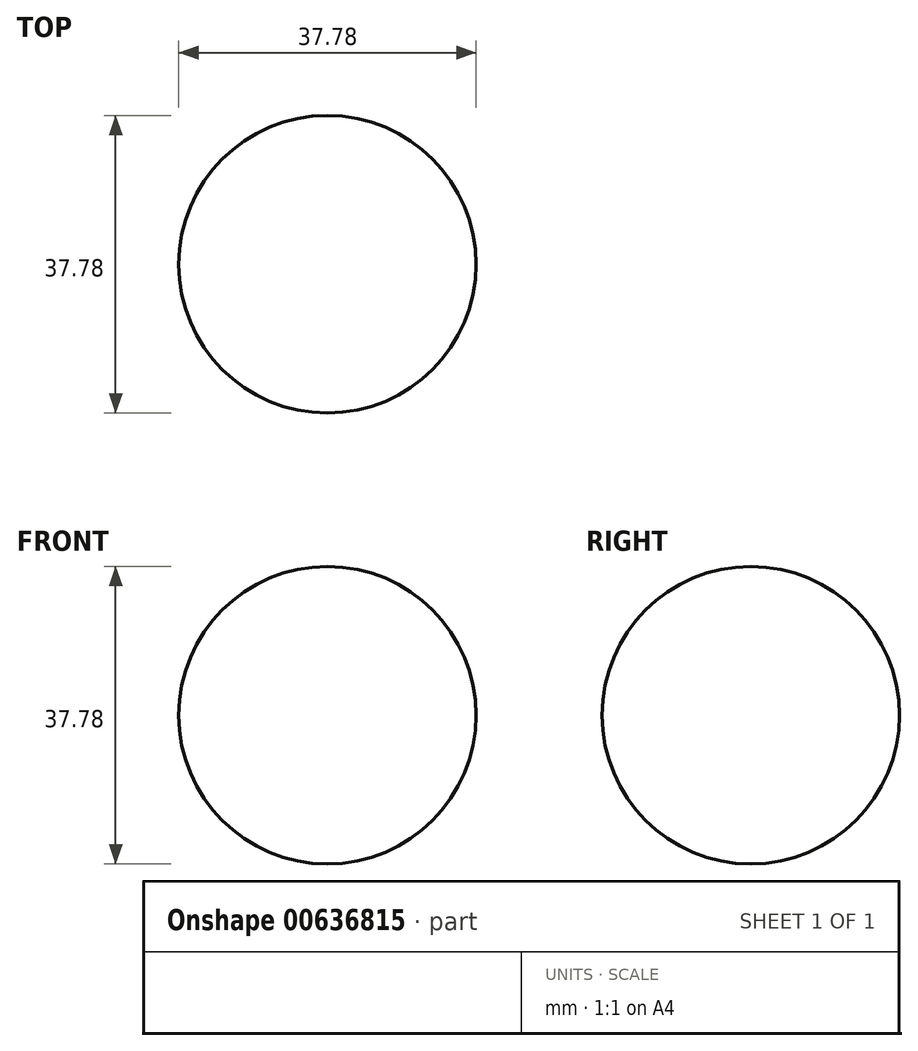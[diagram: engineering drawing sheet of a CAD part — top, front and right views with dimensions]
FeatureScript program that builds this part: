
annotation { "Feature Type Name" : "Feature", "Feature Type Description" : "" }
export const myFeature = defineFeature(function(context is Context, id is Id, definition is map)
    precondition{}
    {
        {
            var Q0;
            Q0=qCreatedBy(makeId("Front.planeOp"),FACE);
            var sketch = newSketch(context, id + "F0", { "sketchPlane" : qUnion([Q0])});
            skArc(sketch, "E0", {"start": v(-18.9, 0) * mm, "mid": v(0, -18.9) * mm, "end": v(18.9, 0) * mm});
            skLineSegment(sketch, "E1", {"start": v(-46.05, 0) * mm, "end": v(46.68, 0) * mm});
            skSolve(sketch);
        }
        {
            var Q0;
            Q0 = qSketchRegion(id + "F0", true);
            var Q1;
            Q1=sQuery(id+"F0.wireOp",EDGE,"E1");
            revolve(context, id + "F1", {"entities" : qUnion([Q0]), "axis" : qUnion([Q1]), "revolveType" : RevolveType.FULL});
        }
    });
